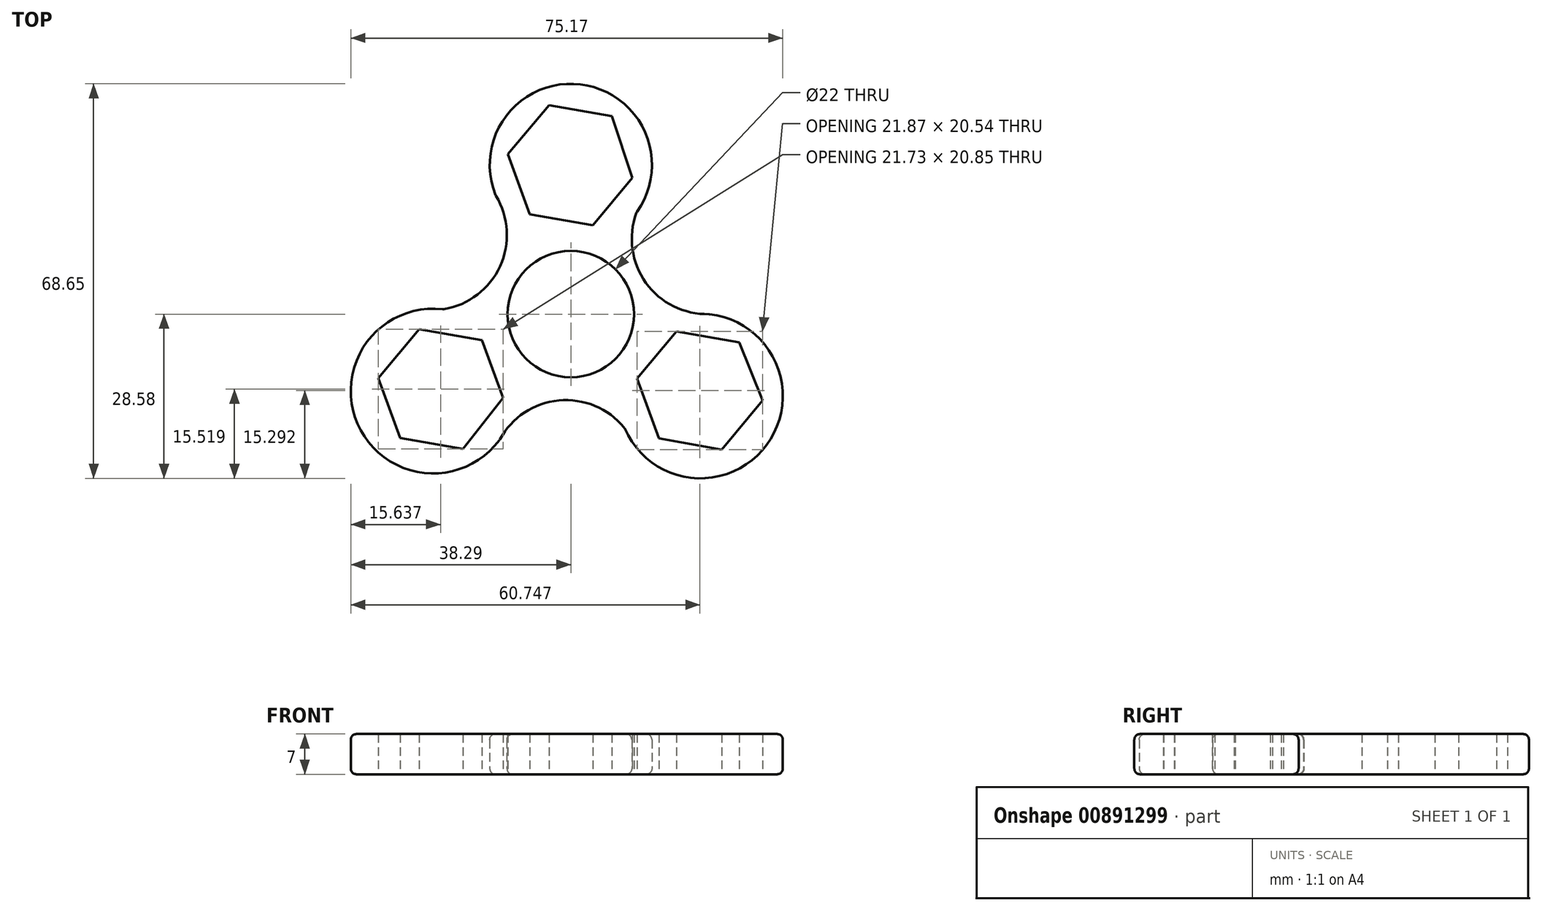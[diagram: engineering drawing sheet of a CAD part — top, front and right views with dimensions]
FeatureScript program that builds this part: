
annotation { "Feature Type Name" : "Feature", "Feature Type Description" : "" }
export const myFeature = defineFeature(function(context is Context, id is Id, definition is map)
    precondition{}
    {
        {
            var Q0;
            Q0=qCreatedBy(makeId("Top.planeOp"),FACE);
            var sketch = newSketch(context, id + "F0", { "sketchPlane" : qUnion([Q0])});
            skCircle(sketch, "E0", {"center": v(0, 0) * mm, "radius": 11 * mm});
            skLineSegment(sketch, "E1.0", {"start": v(-10.93, 27.82) * mm, "end": v(-3.81, 36.33) * mm});
            skLineSegment(sketch, "E1.1", {"start": v(-3.81, 36.33) * mm, "end": v(7.12, 34.42) * mm});
            skLineSegment(sketch, "E1.2", {"start": v(7.12, 34.42) * mm, "end": v(10.68, 23.7) * mm});
            skLineSegment(sketch, "E1.3", {"start": v(10.68, 23.7) * mm, "end": v(3.81, 15.48) * mm});
            skLineSegment(sketch, "E1.4", {"start": v(3.81, 15.48) * mm, "end": v(-7.12, 17.4) * mm});
            skLineSegment(sketch, "E1.5", {"start": v(-7.12, 17.4) * mm, "end": v(-10.93, 27.82) * mm});
            skPoint(sketch, "E1.0.midPoint", {"position": v(-7.37, 32.08) * mm});
            skLineSegment(sketch, "E2.1.0", {"start": v(-18.77, -23.49) * mm, "end": v(-29.7, -21.57) * mm});
            skLineSegment(sketch, "E2.1.1", {"start": v(-11.79, -14.6) * mm, "end": v(-18.77, -23.49) * mm});
            skLineSegment(sketch, "E2.1.2", {"start": v(-15.46, -4.55) * mm, "end": v(-11.79, -14.6) * mm});
            skLineSegment(sketch, "E2.1.4", {"start": v(-26.4, -2.64) * mm, "end": v(-15.46, -4.55) * mm});
            skLineSegment(sketch, "E2.1.5", {"start": v(-33.52, -11.15) * mm, "end": v(-26.4, -2.64) * mm});
            skLineSegment(sketch, "E2.1.6", {"start": v(-29.7, -21.57) * mm, "end": v(-33.52, -11.15) * mm});
            skLineSegment(sketch, "E2.2.0", {"start": v(29.32, -4.93) * mm, "end": v(33.4, -15.05) * mm});
            skLineSegment(sketch, "E2.2.1", {"start": v(18.39, -3.02) * mm, "end": v(29.32, -4.93) * mm});
            skLineSegment(sketch, "E2.2.2", {"start": v(11.52, -11.22) * mm, "end": v(18.39, -3.02) * mm});
            skLineSegment(sketch, "E2.2.4", {"start": v(15.33, -21.65) * mm, "end": v(11.52, -11.22) * mm});
            skLineSegment(sketch, "E2.2.5", {"start": v(26.27, -23.56) * mm, "end": v(15.33, -21.65) * mm});
            skLineSegment(sketch, "E2.2.6", {"start": v(33.4, -15.05) * mm, "end": v(26.27, -23.56) * mm});
            skPoint(sketch, "E2.center", {"position": v(-0.04, -0.1) * mm});
            skPoint(sketch, "E3.center.orphan", {"position": v(0, 25.96) * mm});
            skArc(sketch, "E4", {"start": v(11.45, 17.72) * mm, "mid": v(0.06, 40.07) * mm, "end": v(-11.53, 17.83) * mm});
            skArc(sketch, "E5", {"start": v(-20.84, 0.6) * mm, "mid": v(-36.56, -20.21) * mm, "end": v(-10.54, -18.44) * mm});
            skPoint(sketch, "E6.center", {"position": v(-0.1, -0.05) * mm});
            skArc(sketch, "E7", {"start": v(9.18, -19.43) * mm, "mid": v(34.87, -21.56) * mm, "end": v(20.69, -0.04) * mm});
            skArc(sketch, "E8", {"start": v(-22.2, 0.84) * mm, "mid": v(-12.32, 8.3) * mm, "end": v(-13.07, 20.66) * mm});
            skArc(sketch, "E9.1.0", {"start": v(9.35, -19.85) * mm, "mid": v(-2.06, -15.02) * mm, "end": v(-12.38, -21.85) * mm});
            skArc(sketch, "E9.2.0", {"start": v(11.49, 17.82) * mm, "mid": v(13.01, 5.53) * mm, "end": v(24.09, 0) * mm});
            skPoint(sketch, "E9.center", {"position": v(-0.46, -0.4) * mm});
            skSolve(sketch);
        }
        {
            var Q0;
            Q0=makeQuery(id+"F0.imprint","IMPRINT",FACE,{"disambiguationData":[TD([[makeQuery(id+"F0.imprint","IMPRINT",EDGE,{"derivedFrom":sQuery(id+"F0.wireOp",EDGE,"E0")}),-1.0]])]});
            extrude(context, id + "F1", {"entities" : qUnion([Q0]), "depth" : 7 * mm, "offsetDistance" : 25 * mm});
        }
        {
            var Q0;
            Q0=makeQuery(id+"F1.opExtrude","SWEPT_FACE",FACE,{"disambiguationData":[OSD([sQuery(id+"F0.wireOp",EDGE,"E8")])]});
            var Q1;
            Q1=makeQuery(id+"F1.opExtrude","SWEPT_FACE",FACE,{"disambiguationData":[OSD([sQuery(id+"F0.wireOp",EDGE,"E4")])]});
            var Q2;
            Q2=makeQuery(id+"F1.opExtrude","CAP_EDGE",EDGE,{"disambiguationData":[OSD([sQuery(id+"F0.wireOp",EDGE,"E9.2.0")])],"isStart":true});
            var Q3;
            Q3=makeQuery(id+"F1.opExtrude","SWEPT_FACE",FACE,{"disambiguationData":[OSD([sQuery(id+"F0.wireOp",EDGE,"E9.2.0")])]});
            var Q4;
            Q4=makeQuery(id+"F1.opExtrude","SWEPT_FACE",FACE,{"disambiguationData":[OSD([sQuery(id+"F0.wireOp",EDGE,"E7")])]});
            var Q5;
            Q5=makeQuery(id+"F1.opExtrude","SWEPT_FACE",FACE,{"disambiguationData":[OSD([sQuery(id+"F0.wireOp",EDGE,"E5")])]});
            var Q6;
            Q6=makeQuery(id+"F1.opExtrude","SWEPT_FACE",FACE,{"disambiguationData":[OSD([sQuery(id+"F0.wireOp",EDGE,"E9.1.0")])]});
            fillet(context, id + "F2", {"entities" : qUnion([Q0, Q1, Q2, Q3, Q4, Q5, Q6]), "radius" : 1 * mm, "tangentPropagation" : true, "allowEdgeOverflow" : false});
        }
    });
